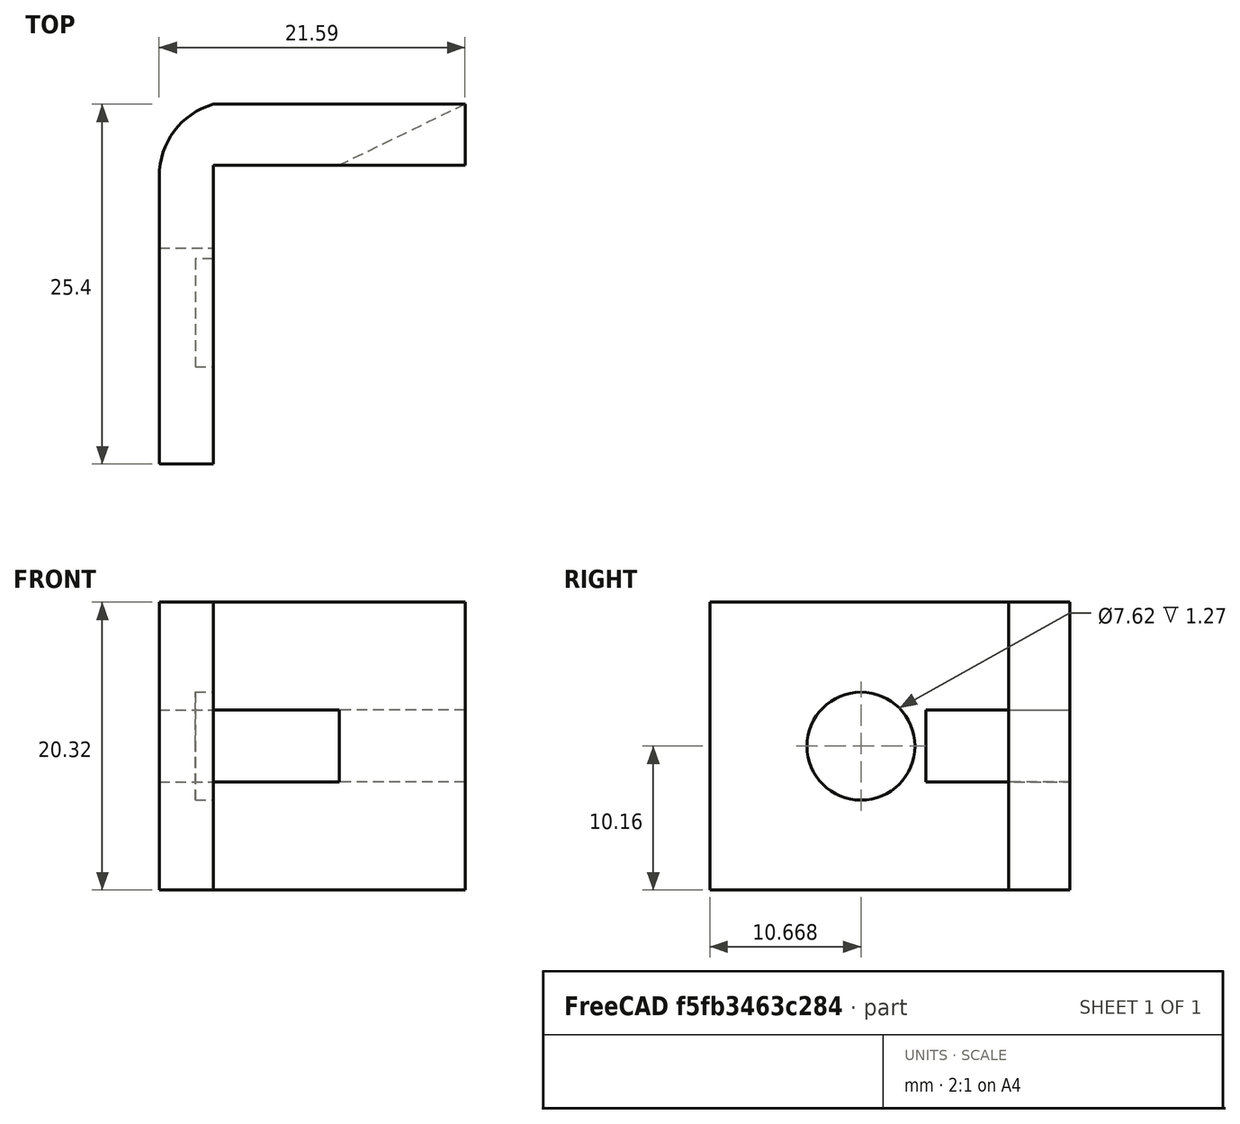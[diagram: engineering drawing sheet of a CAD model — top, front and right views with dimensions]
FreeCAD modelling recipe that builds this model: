
FCSTD DOCUMENT  (FreeCAD 0.18.1R)
Label: thumb_plate_rev_02
License: All rights reserved
LicenseURL: http://en.wikipedia.org/wiki/All_rights_reserved
objects: Sketcher::SketchObject×6, PartDesign::Pocket×4, PartDesign::Pad×2, PartDesign::Body×1, Mesh::Feature×1
note: 19 computed .brp shape members not serialized (recipe doc carries the construction recipe); baked Part::Feature solids carry a one-line shape summary decoded from their .brp

FEATURE [Sketcher::SketchObject] Sketch
  MapMode = 5
  Support = -> [XY_Plane]
  sketch-geometry (5):
    g0: LineSegment StartX=0 StartY=0 StartZ=0 EndX=1.905 EndY=0 EndZ=0
    g1: LineSegment StartX=1.905 StartY=0 StartZ=0 EndX=1.905 EndY=25.4 EndZ=0
    g2: LineSegment StartX=-1.905 StartY=0 StartZ=0 EndX=0 EndY=0 EndZ=0
    g3: LineSegment StartX=-1.905 StartY=0 StartZ=0 EndX=-1.905 EndY=20.32 EndZ=0
    g4: ArcOfCircle CenterX=3.38667 CenterY=20.32 CenterZ=0 NormalX=0 NormalY=0 NormalZ=1 AngleXU=0 Radius=5.29167 StartAngle=1.85459 EndAngle=3.14159
  constraints (15):
    c: Coincident(g0,g-1)
    c: PointOnObject(g0,g-1)
    c: Coincident(g1,g0)
    c: Vertical(g1)
    c: PointOnObject(g2,g-1)
    c: Coincident(g2,g0)
    c: DistanceY(g1,g1) = 25.4
    c: Coincident(g3,g2)
    c: Vertical(g3)
    c: Coincident(g4,g3)
    c: Coincident(g4,g1)
    c: DistanceY(g3,g3) = 20.32
    c: Distance(g4,g0) = 20.32
    c: Distance(g3,g1) = 3.81
    c: DistanceX(g0,g0) = 1.905
FEATURE [PartDesign::Pad] Pad
  Length = 25.4
  Length2 = 100.076
  Profile = -> Sketch
  Type = 0
FEATURE [Sketcher::SketchObject] Sketch001
  MapMode = 5
  Placement = pos=(1.905,0,0) rot=(0.57735,0.57735,0.57735;2.0944rad)
  Support = -> [Pad]
  sketch-geometry (4):
    g0: LineSegment StartX=25.4 StartY=0 StartZ=0 EndX=25.4 EndY=25.4 EndZ=0
    g1: LineSegment StartX=25.4 StartY=25.4 StartZ=0 EndX=21.082 EndY=25.4 EndZ=0
    g2: LineSegment StartX=21.082 StartY=25.4 StartZ=0 EndX=21.082 EndY=0 EndZ=0
    g3: LineSegment StartX=21.082 StartY=0 StartZ=0 EndX=25.4 EndY=0 EndZ=0
  constraints (12):
    c: PointOnObject(g0,g-1)
    c: Vertical(g0)
    c: Coincident(g1,g0)
    c: Horizontal(g1)
    c: Coincident(g2,g1)
    c: PointOnObject(g2,g-1)
    c: Vertical(g2)
    c: Coincident(g3,g2)
    c: Coincident(g3,g0)
    c: DistanceX(g1,g1) = 4.318
    c: Distance(g0,g-1) = 25.4
    c: Distance(g0) = 25.4
FEATURE [PartDesign::Pad] Pad001
  BaseFeature = -> Pad
  Length = 17.78
  Length2 = 100.076
  Profile = -> Sketch001
  Type = 0
FEATURE [Sketcher::SketchObject] Sketch002
  MapMode = 5
  Placement = pos=(-1.905,0,0) rot=(0.57735,-0.57735,-0.57735;2.0944rad)
  Support = -> [Pad001]
  sketch-geometry (4):
    g0: LineSegment StartX=-25.4 StartY=10.16 StartZ=0 EndX=-15.24 EndY=10.16 EndZ=0
    g1: LineSegment StartX=-15.24 StartY=10.16 StartZ=0 EndX=-15.24 EndY=15.24 EndZ=0
    g2: LineSegment StartX=-15.24 StartY=15.24 StartZ=0 EndX=-25.4 EndY=15.24 EndZ=0
    g3: LineSegment StartX=-25.4 StartY=15.24 StartZ=0 EndX=-25.4 EndY=10.16 EndZ=0
  constraints (12):
    c: Coincident(g0,g1)
    c: Coincident(g1,g2)
    c: Coincident(g2,g3)
    c: Coincident(g3,g0)
    c: Horizontal(g0)
    c: Horizontal(g2)
    c: Vertical(g1)
    c: Vertical(g3)
    c: Distance(g0,g-2) = 25.4
    c: Distance(g0,g-1) = 10.16
    c: DistanceY(g3,g3) = 5.08
    c: DistanceX(g2,g2) = 10.16
FEATURE [PartDesign::Pocket] Pocket
  BaseFeature = -> Pad001
  Length = 12.7
  Length2 = 100.076
  Profile = -> Sketch002
  Type = 0
FEATURE [Sketcher::SketchObject] Sketch003
  MapMode = 5
  Placement = pos=(1.905,0,0) rot=(0.57735,0.57735,0.57735;2.0944rad)
  Support = -> [Pocket]
  sketch-geometry (1):
    g0: Circle CenterX=10.668 CenterY=12.7 CenterZ=0 NormalX=0 NormalY=0 NormalZ=1 AngleXU=0 Radius=3.81
  constraints (3):
    c: Radius(g0) = 3.81
    c: Distance(g0,g-1) = 12.7
    c: Distance(g0,g-2) = 10.668
FEATURE [PartDesign::Pocket] Pocket001
  BaseFeature = -> Pocket
  Length = 1.27
  Length2 = 100.076
  Profile = -> Sketch003
  Type = 0
FEATURE [Sketcher::SketchObject] Sketch004
  MapMode = 5
  Placement = pos=(19.685,0,0) rot=(0.57735,0.57735,0.57735;2.0944rad)
  Support = -> [Pocket001]
  sketch-geometry (8):
    g0: LineSegment StartX=0 StartY=0 StartZ=0 EndX=25.4 EndY=0 EndZ=0
    g1: LineSegment StartX=25.4 StartY=0 StartZ=0 EndX=25.4 EndY=2.54 EndZ=0
    g2: LineSegment StartX=25.4 StartY=2.54 StartZ=0 EndX=0 EndY=2.54 EndZ=0
    g3: LineSegment StartX=0 StartY=2.54 StartZ=0 EndX=0 EndY=0 EndZ=0
    g4: LineSegment StartX=0 StartY=25.4 StartZ=0 EndX=25.4 EndY=25.4 EndZ=0
    g5: LineSegment StartX=25.4 StartY=25.4 StartZ=0 EndX=25.4 EndY=22.86 EndZ=0
    g6: LineSegment StartX=25.4 StartY=22.86 StartZ=0 EndX=0 EndY=22.86 EndZ=0
    g7: LineSegment StartX=0 StartY=22.86 StartZ=0 EndX=0 EndY=25.4 EndZ=0
  constraints (23):
    c: Coincident(g0,g1)
    c: Coincident(g1,g2)
    c: Coincident(g2,g3)
    c: Coincident(g3,g0)
    c: Horizontal(g0)
    c: Horizontal(g2)
    c: Vertical(g1)
    c: Vertical(g3)
    c: Coincident(g0,g-1)
    c: Coincident(g4,g5)
    c: Coincident(g5,g6)
    c: Coincident(g6,g7)
    c: Coincident(g7,g4)
    c: Horizontal(g4)
    c: Horizontal(g6)
    c: Vertical(g5)
    c: Vertical(g7)
    c: PointOnObject(g4,g-2)
    c: Distance(g2) = 25.4
    c: Distance(g1) = 2.54
    c: Distance(g7) = 2.54
    c: Distance(g4) = 25.4
    c: Distance(g6,g0) = 22.86
FEATURE [PartDesign::Pocket] Pocket002
  BaseFeature = -> Pocket001
  Length = 30.48
  Length2 = 100.076
  Profile = -> Sketch004
  Type = 0
FEATURE [Sketcher::SketchObject] Sketch005
  MapMode = 5
  Placement = pos=(0,0,10.16) rot=(0,0,1;0rad)
  Support = -> [Pocket002]
  sketch-geometry (3):
    g0: LineSegment StartX=19.685 StartY=25.4 StartZ=0 EndX=10.795 EndY=25.4 EndZ=0
    g1: LineSegment StartX=10.795 StartY=25.4 StartZ=0 EndX=10.795 EndY=21.082 EndZ=0
    g2: LineSegment StartX=19.685 StartY=25.4 StartZ=0 EndX=10.795 EndY=21.082 EndZ=0
  constraints (9):
    c: Horizontal(g0)
    c: DistanceX(g0,g0) = 8.89
    c: Coincident(g1,g0)
    c: Vertical(g1)
    c: DistanceY(g1,g1) = 4.318
    c: Distance(g1,g-1) = 21.082
    c: Distance(g1,g-2) = 10.795
    c: Coincident(g2,g0)
    c: Coincident(g2,g1)
FEATURE [PartDesign::Pocket] Pocket003
  BaseFeature = -> Pocket002
  Length = 5.08
  Length2 = 100.076
  Profile = -> Sketch005
  Reversed = true
  Type = 0
FEATURE [PartDesign::Body] Body
  Group = -> [Sketch,Pad,Sketch001,Pad001,Sketch002,Pocket,Sketch003,Pocket001,Sketch004,Pocket002,Sketch005,Pocket003]
  Origin = -> Origin
  Tip = -> Pocket003
FEATURE [Mesh::Feature] Mesh  label="Body (Meshed)"
